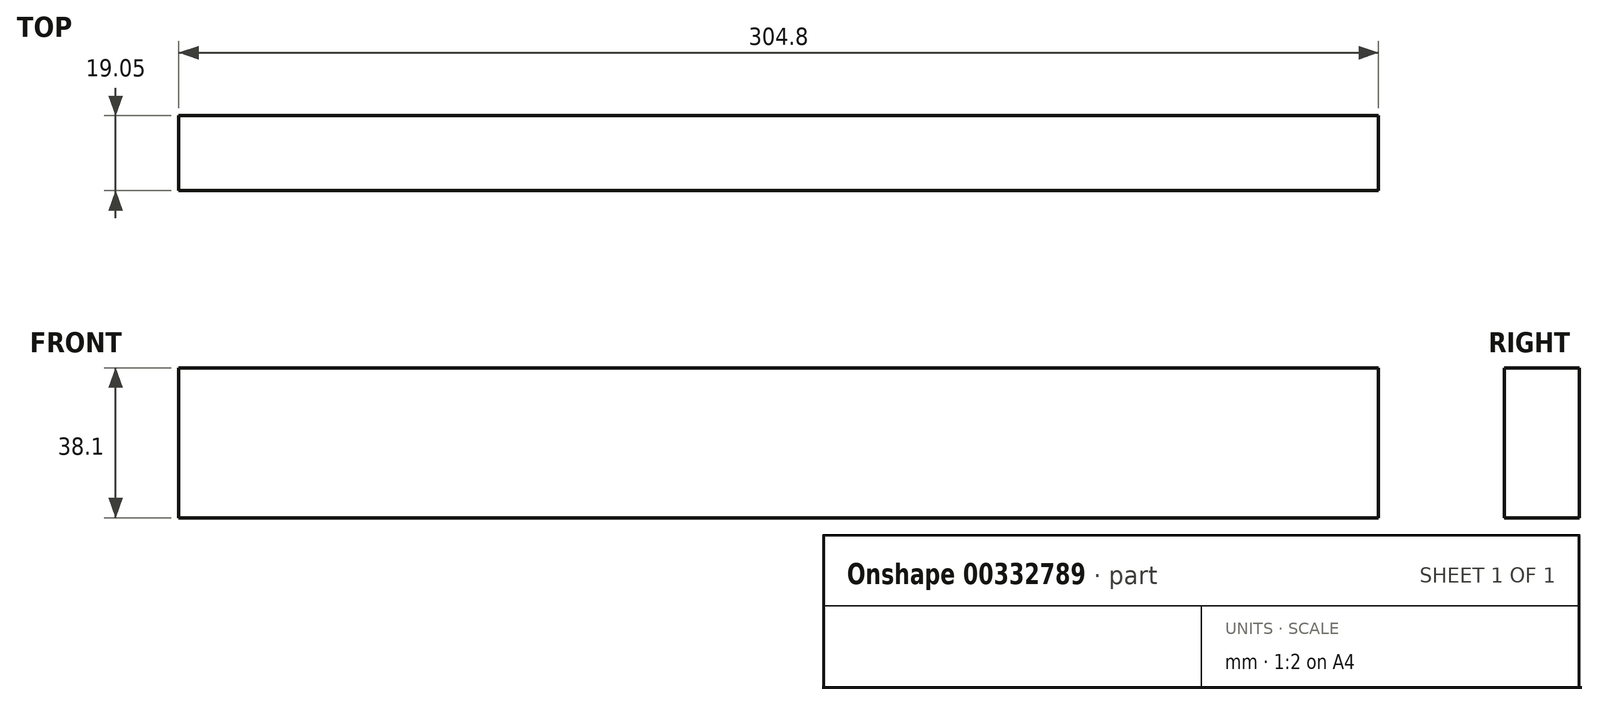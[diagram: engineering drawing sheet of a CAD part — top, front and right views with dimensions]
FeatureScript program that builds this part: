
annotation { "Feature Type Name" : "Feature", "Feature Type Description" : "" }
export const myFeature = defineFeature(function(context is Context, id is Id, definition is map)
    precondition{}
    {
        {
            var Q0;
            Q0=qCreatedBy(makeId("Front.planeOp"),FACE);
            var sketch = newSketch(context, id + "F0", { "sketchPlane" : qUnion([Q0])});
            skLineSegment(sketch, "E0.bottom", {"start": v(152.4, 19.05) * mm, "end": v(-152.4, 19.05) * mm});
            skLineSegment(sketch, "E0.top", {"start": v(152.4, -19.05) * mm, "end": v(-152.4, -19.05) * mm});
            skLineSegment(sketch, "E0.left", {"start": v(152.4, 19.05) * mm, "end": v(152.4, -19.05) * mm});
            skLineSegment(sketch, "E0.right", {"start": v(-152.4, 19.05) * mm, "end": v(-152.4, -19.05) * mm});
            skPoint(sketch, "E0.middle", {"position": v(0, 0) * mm});
            skSolve(sketch);
        }
        {
            var Q0;
            Q0=makeQuery(id+"F0.imprint","IMPRINT",FACE,{"disambiguationData":[TD([[makeQuery(id+"F0.imprint","IMPRINT",EDGE,{"derivedFrom":sQuery(id+"F0.wireOp",EDGE,"E0.bottom")}),1.0]])]});
            extrude(context, id + "F1", {"entities" : qUnion([Q0]), "depth" : 19.05 * mm});
        }
    });
